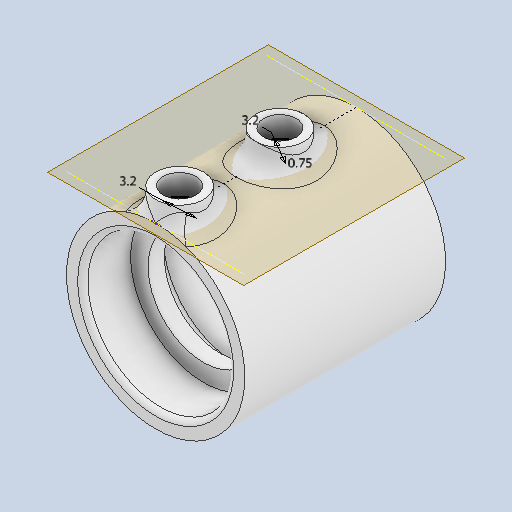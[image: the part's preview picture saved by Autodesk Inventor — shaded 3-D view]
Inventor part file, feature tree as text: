
AUTODESK INVENTOR PART (.ipt)
format: ipt  version: 2023 (Build 270158000, 158)  size: 397,312 bytes
history: native  units: mm
features: extrude x5, fillet x4, sketch x3, chamfer x1, plane x1
ambient origin geometry x8: Origin, YZ Plane, XZ Plane, XY Plane, X Axis, Y Axis, Z Axis, Center Point
bodies: Solid1 (feature_tree)
feature tree (14):
  extrude  "Extrusion1"  Depth=1.6mm
  extrude  "Extrusion2"  Depth=4.7mm
  chamfer  "Chamfer1"  Distance=1.6mm
  plane  "Work Plane1"
  sketch  "Sketch3"  dims[d7=15.0mm d8=0.0mm d10=1.6mm d11=2.0mm d12=45.0deg d13=3.2mm d14=3.2mm d15=0.75mm d16=2.0mm d17=0.5mm d18=0.0mm d19=0.0mm d20=2.0mm d21=0.5mm d22=0.0mm d23=0.0mm d24=2.0mm d25=0.0mm d26=2.0mm d27=2.0mm d28=0.5mm d29=0.5mm]
  extrude  "Extrusion3"  Depth=0.5mm
  extrude  "Extrusion4"  Depth=0.5mm
  extrude  "Extrusion5"  Depth=0.5mm
  fillet  "Fillet2"  Radius=0.5mm
  fillet  "Fillet3"  Radius=0.5mm
  fillet  "Fillet4"  Radius=2.0mm
  fillet  "Fillet5"  Radius=2.0mm
  sketch  "Sketch1"  dims[d0=14.3mm d1=1.6mm]
  sketch  "Sketch2"  dims[d2=4.7mm d3=0.0mm d4=3.2mm d5=1.6mm d6=0.0mm]
